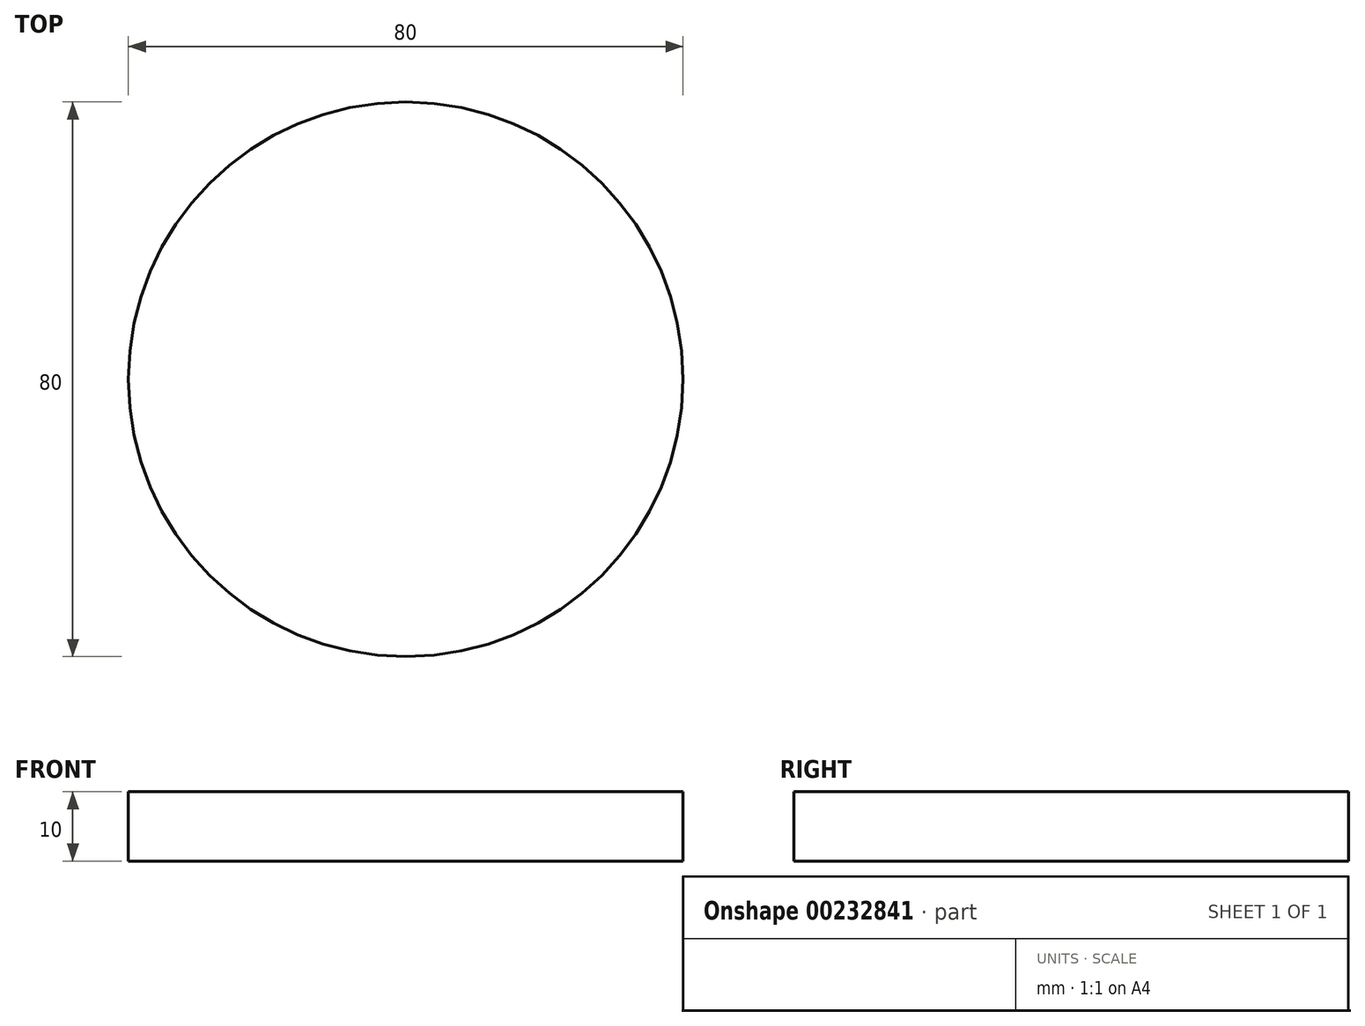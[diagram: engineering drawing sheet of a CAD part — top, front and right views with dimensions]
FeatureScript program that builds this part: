
annotation { "Feature Type Name" : "Feature", "Feature Type Description" : "" }
export const myFeature = defineFeature(function(context is Context, id is Id, definition is map)
    precondition{}
    {
        {
            var Q0;
            Q0=qCreatedBy(makeId("Top.planeOp"),FACE);
            var sketch = newSketch(context, id + "F0", { "sketchPlane" : qUnion([Q0])});
            skCircle(sketch, "E0", {"center": v(0, 0) * mm, "radius": 40 * mm});
            skSolve(sketch);
        }
        {
            var Q0;
            Q0=makeQuery(id+"F0.imprint","IMPRINT",FACE,{"disambiguationData":[TD([[makeQuery(id+"F0.imprint","IMPRINT",EDGE,{"derivedFrom":sQuery(id+"F0.wireOp",EDGE,"E0")}),1.0]])]});
            extrude(context, id + "F1", {"entities" : qUnion([Q0]), "oppositeDirection" : true, "depth" : 10 * mm});
        }
        {
            var Q0;
            Q0=makeQuery(id+"F1.opExtrude","CAP_FACE",FACE,{"disambiguationData":[OSD([sQuery(id+"F0.wireOp",EDGE,"E0")])],"isStart":true});
            var sketch = newSketch(context, id + "F2", { "sketchPlane" : qUnion([Q0])});
            skCircle(sketch, "E1", {"center": v(-9.73, 21.18) * mm, "radius": 7.5 * mm});
            skCircle(sketch, "E2", {"center": v(11.7, 19.52) * mm, "radius": 7.5 * mm});
            skArc(sketch, "E3", {"start": v(-24.8, -3.16) * mm, "mid": v(-2.8, -24.84) * mm, "end": v(23.47, -8.61) * mm});
            skSolve(sketch);
        }
        {
            var Q0;
            Q0=makeQuery(id+"F2.imprint","IMPRINT",FACE,{"disambiguationData":[TD([[makeQuery(id+"F2.imprint","IMPRINT",EDGE,{"derivedFrom":sQuery(id+"F2.wireOp",EDGE,"E1")}),1.0]])]});
            var Q1;
            Q1=makeQuery(id+"F2.imprint","IMPRINT",FACE,{"disambiguationData":[TD([[makeQuery(id+"F2.imprint","IMPRINT",EDGE,{"derivedFrom":sQuery(id+"F2.wireOp",EDGE,"E2")}),1.0]])]});
            var Q2;
            Q2=makeQuery(id+"F2.imprint","IMPRINT",FACE,{"disambiguationData":[TD([[makeQuery(id+"F2.imprint","IMPRINT",EDGE,{"derivedFrom":sQuery(id+"F2.wireOp",EDGE,"E1")}),-1.0]])]});
            var Q3;
            Q3=sQuery(id+"F2.wireOp",EDGE,"E1");
            var Q4;
            Q4=sQuery(id+"F2.wireOp",EDGE,"E2");
            var Q5;
            Q5=sQuery(id+"F2.wireOp",EDGE,"E3");
            extrude(context, id + "F3", {"entities" : qUnion([Q0, Q1, Q2]), "bodyType" : ToolBodyType.SURFACE, "surfaceEntities" : qUnion([Q3, Q4, Q5]), "endBound" : BoundingType.SYMMETRIC, "oppositeDirection" : true, "depth" : 20 * mm});
        }
    });
